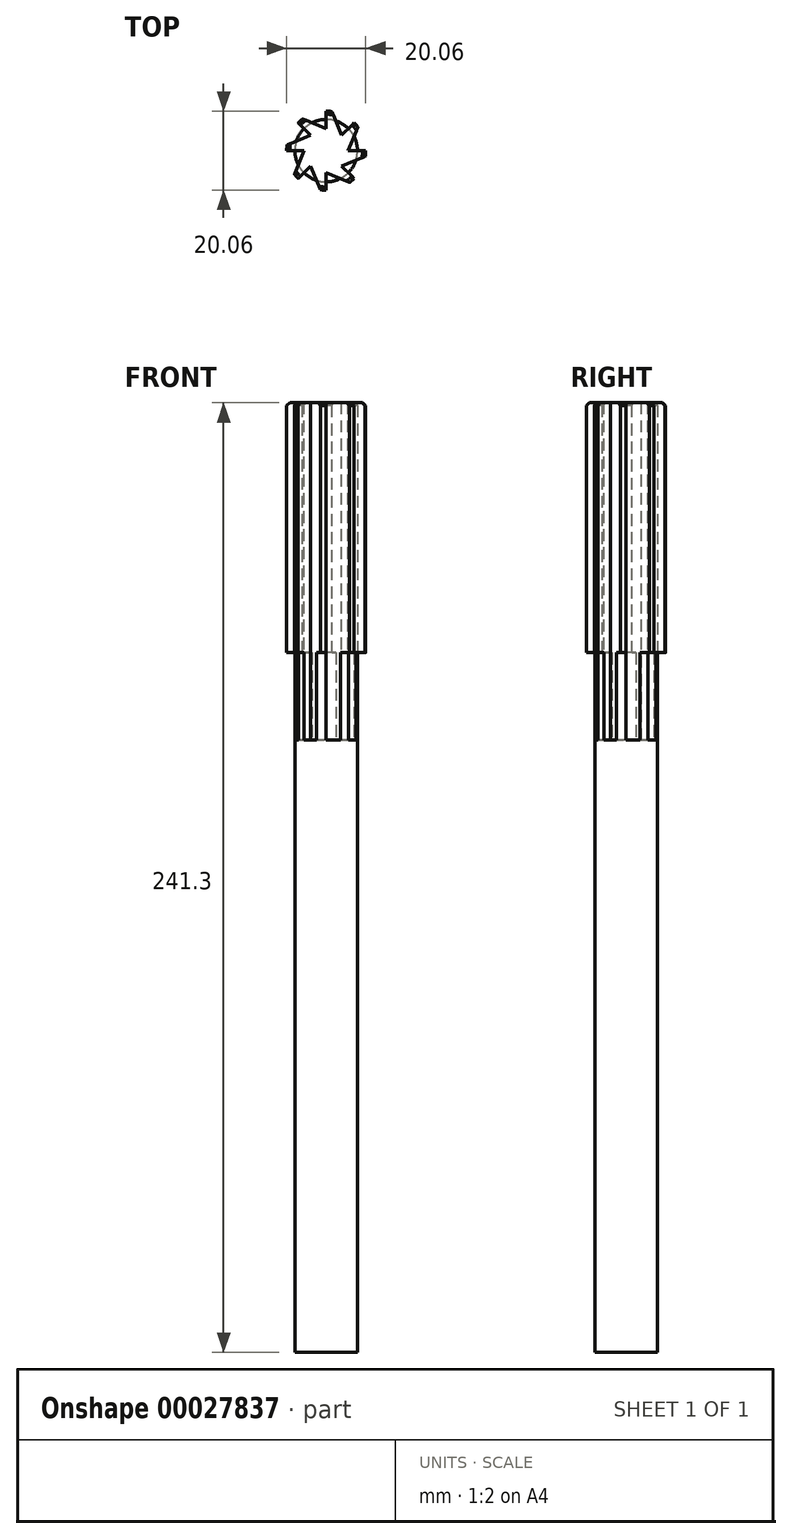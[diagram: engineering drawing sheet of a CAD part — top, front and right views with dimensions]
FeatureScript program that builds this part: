
annotation { "Feature Type Name" : "Feature", "Feature Type Description" : "" }
export const myFeature = defineFeature(function(context is Context, id is Id, definition is map)
    precondition{}
    {
        {
            var Q0;
            Q0=qCreatedBy(makeId("Top.planeOp"),FACE);
            var sketch = newSketch(context, id + "F0", { "sketchPlane" : qUnion([Q0])});
            skCircle(sketch, "E0", {"center": v(0, 0) * mm, "radius": 7.94 * mm});
            skSolve(sketch);
        }
        {
            var Q0;
            Q0 = qSketchRegion(id + "F0", true);
            extrude(context, id + "F1", {"entities" : qUnion([Q0]), "endBound" : BoundingType.SYMMETRIC, "depth" : 241.3 * mm});
        }
        {
            var Q0;
            Q0=makeQuery(id+"F1.opExtrude","CAP_FACE",FACE,{"disambiguationData":[OSD([sQuery(id+"F0.wireOp",EDGE,"E0")])],"isStart":false});
            var sketch = newSketch(context, id + "F2", { "sketchPlane" : qUnion([Q0])});
            skCircle(sketch, "E1", {"center": v(0, 0) * mm, "radius": 10.03 * mm});
            skSolve(sketch);
        }
        {
            var Q0;
            Q0 = qSketchRegion(id + "F2", true);
            extrude(context, id + "F3", {"entities" : qUnion([Q0]), "operationType" : NewBodyOperationType.ADD, "oppositeDirection" : true, "depth" : 63.5 * mm});
        }
        {
            var Q0;
            Q0=makeQuery(id+"F3.boolean.opBoolean","MERGE",FACE,{"derivedFrom":[makeQuery(id+"F1.opExtrude","CAP_FACE",FACE,{"disambiguationData":[OSD([sQuery(id+"F0.wireOp",EDGE,"E0")])],"isStart":false}),makeQuery(id+"F3.opExtrude","CAP_FACE",FACE,{"disambiguationData":[OSD([sQuery(id+"F2.wireOp",EDGE,"E1")])],"isStart":true})]});
            var sketch = newSketch(context, id + "F4", { "sketchPlane" : qUnion([Q0])});
            skLineSegment(sketch, "E2", {"start": v(0, 5.58) * mm, "end": v(0, 12.7) * mm});
            skLineSegment(sketch, "E3", {"start": v(0.33, 12.7) * mm, "end": v(3.95, 3.95) * mm});
            skArc(sketch, "E4", {"start": v(8.98, 8.98) * mm, "mid": v(5.01, 11.67) * mm, "end": v(0.33, 12.7) * mm});
            skLineSegment(sketch, "E5.1.0", {"start": v(-8.75, 9.2) * mm, "end": v(0, 5.58) * mm});
            skLineSegment(sketch, "E5.1.1", {"start": v(-3.95, 3.95) * mm, "end": v(-8.98, 8.98) * mm});
            skLineSegment(sketch, "E5.2.0", {"start": v(-12.7, 0.33) * mm, "end": v(-3.95, 3.95) * mm});
            skLineSegment(sketch, "E5.2.1", {"start": v(-5.58, 0) * mm, "end": v(-12.7, 0) * mm});
            skLineSegment(sketch, "E5.3.0", {"start": v(-9.2, -8.75) * mm, "end": v(-5.58, 0) * mm});
            skLineSegment(sketch, "E5.3.1", {"start": v(-3.95, -3.95) * mm, "end": v(-8.98, -8.98) * mm});
            skLineSegment(sketch, "E5.4.0", {"start": v(-0.33, -12.7) * mm, "end": v(-3.95, -3.95) * mm});
            skLineSegment(sketch, "E5.4.1", {"start": v(0, -5.58) * mm, "end": v(0, -12.7) * mm});
            skLineSegment(sketch, "E5.5.0", {"start": v(8.75, -9.2) * mm, "end": v(0, -5.58) * mm});
            skLineSegment(sketch, "E5.5.1", {"start": v(3.95, -3.95) * mm, "end": v(8.98, -8.98) * mm});
            skLineSegment(sketch, "E5.6.0", {"start": v(12.7, -0.33) * mm, "end": v(3.95, -3.95) * mm});
            skLineSegment(sketch, "E5.6.1", {"start": v(5.58, 0) * mm, "end": v(12.7, 0) * mm});
            skLineSegment(sketch, "E5.7.0", {"start": v(9.2, 8.75) * mm, "end": v(5.58, 0) * mm});
            skLineSegment(sketch, "E5.7.1", {"start": v(3.95, 3.95) * mm, "end": v(8.98, 8.98) * mm});
            skPoint(sketch, "E6.orphan", {"position": v(-5.58, 0) * mm});
            skArc(sketch, "E7.trimOffspring", {"start": v(-12.7, 0) * mm, "mid": v(-11.8, -4.7) * mm, "end": v(-9.2, -8.75) * mm});
            skArc(sketch, "E8.trimOffspring", {"start": v(0, 12.7) * mm, "mid": v(-4.7, 11.8) * mm, "end": v(-8.75, 9.2) * mm});
            skArc(sketch, "E9.trimOffspring", {"start": v(-8.98, 8.98) * mm, "mid": v(-11.67, 5.01) * mm, "end": v(-12.7, 0.33) * mm});
            skArc(sketch, "E10.trimOffspring", {"start": v(12.7, 0) * mm, "mid": v(11.8, 4.7) * mm, "end": v(9.2, 8.75) * mm});
            skArc(sketch, "E11.trimOffspring", {"start": v(8.98, -8.98) * mm, "mid": v(11.67, -5.01) * mm, "end": v(12.7, -0.33) * mm});
            skArc(sketch, "E12.trimOffspring", {"start": v(0, -12.7) * mm, "mid": v(4.7, -11.8) * mm, "end": v(8.75, -9.2) * mm});
            skArc(sketch, "E13.trimOffspring", {"start": v(-8.98, -8.98) * mm, "mid": v(-5.01, -11.67) * mm, "end": v(-0.33, -12.7) * mm});
            skLineSegment(sketch, "E14", {"start": v(3.95, 3.95) * mm, "end": v(5.58, 0) * mm, "construction": true});
            skSolve(sketch);
        }
        {
            var Q0;
            Q0 = qSketchRegion(id + "F4", true);
            extrude(context, id + "F5", {"entities" : qUnion([Q0]), "operationType" : NewBodyOperationType.REMOVE, "oppositeDirection" : true, "depth" : 85.72 * mm});
        }
        {
            var Q0;
            {var subQ0=sQuery(id+"F2.wireOp",EDGE,"E1");Q0=makeQuery(id+"F5.boolean.opBoolean","SPLIT",EDGE,{"disambiguationData":[TD([makeQuery(id+"F5.opExtrude","SWEPT_FACE",FACE,{"disambiguationData":[OSD([sQuery(id+"F4.wireOp",EDGE,"E5.1.0")])]})])],"derivedFrom":makeQuery(id+"F3.opExtrude","CAP_EDGE",EDGE,{"disambiguationData":[OSD([subQ0])],"isStart":true})});}
            var Q1;
            {var subQ0=sQuery(id+"F2.wireOp",EDGE,"E1");Q1=makeQuery(id+"F5.boolean.opBoolean","SPLIT",EDGE,{"disambiguationData":[TD([makeQuery(id+"F5.opExtrude","SWEPT_FACE",FACE,{"disambiguationData":[OSD([sQuery(id+"F4.wireOp",EDGE,"E5.2.0")])]})])],"derivedFrom":makeQuery(id+"F3.opExtrude","CAP_EDGE",EDGE,{"disambiguationData":[OSD([subQ0])],"isStart":true})});}
            var Q2;
            {var subQ0=sQuery(id+"F2.wireOp",EDGE,"E1");Q2=makeQuery(id+"F5.boolean.opBoolean","SPLIT",EDGE,{"disambiguationData":[TD([makeQuery(id+"F5.opExtrude","SWEPT_FACE",FACE,{"disambiguationData":[OSD([sQuery(id+"F4.wireOp",EDGE,"E2")])]})])],"derivedFrom":makeQuery(id+"F3.opExtrude","CAP_EDGE",EDGE,{"disambiguationData":[OSD([subQ0])],"isStart":true})});}
            var Q3;
            {var subQ0=sQuery(id+"F2.wireOp",EDGE,"E1");Q3=makeQuery(id+"F5.boolean.opBoolean","SPLIT",EDGE,{"disambiguationData":[TD([makeQuery(id+"F5.opExtrude","SWEPT_FACE",FACE,{"disambiguationData":[OSD([sQuery(id+"F4.wireOp",EDGE,"E5.7.0")])]})])],"derivedFrom":makeQuery(id+"F3.opExtrude","CAP_EDGE",EDGE,{"disambiguationData":[OSD([subQ0])],"isStart":true})});}
            var Q4;
            {var subQ0=sQuery(id+"F2.wireOp",EDGE,"E1");Q4=makeQuery(id+"F5.boolean.opBoolean","SPLIT",EDGE,{"disambiguationData":[TD([makeQuery(id+"F5.opExtrude","SWEPT_FACE",FACE,{"disambiguationData":[OSD([sQuery(id+"F4.wireOp",EDGE,"E5.6.0")])]})])],"derivedFrom":makeQuery(id+"F3.opExtrude","CAP_EDGE",EDGE,{"disambiguationData":[OSD([subQ0])],"isStart":true})});}
            var Q5;
            {var subQ0=sQuery(id+"F2.wireOp",EDGE,"E1");Q5=makeQuery(id+"F5.boolean.opBoolean","SPLIT",EDGE,{"disambiguationData":[TD([makeQuery(id+"F5.opExtrude","SWEPT_FACE",FACE,{"disambiguationData":[OSD([sQuery(id+"F4.wireOp",EDGE,"E5.5.0")])]})])],"derivedFrom":makeQuery(id+"F3.opExtrude","CAP_EDGE",EDGE,{"disambiguationData":[OSD([subQ0])],"isStart":true})});}
            var Q6;
            {var subQ0=sQuery(id+"F2.wireOp",EDGE,"E1");Q6=makeQuery(id+"F5.boolean.opBoolean","SPLIT",EDGE,{"disambiguationData":[TD([makeQuery(id+"F5.opExtrude","SWEPT_FACE",FACE,{"disambiguationData":[OSD([sQuery(id+"F4.wireOp",EDGE,"E5.4.0")])]})])],"derivedFrom":makeQuery(id+"F3.opExtrude","CAP_EDGE",EDGE,{"disambiguationData":[OSD([subQ0])],"isStart":true})});}
            var Q7;
            {var subQ0=sQuery(id+"F2.wireOp",EDGE,"E1");Q7=makeQuery(id+"F5.boolean.opBoolean","SPLIT",EDGE,{"disambiguationData":[TD([makeQuery(id+"F5.opExtrude","SWEPT_FACE",FACE,{"disambiguationData":[OSD([sQuery(id+"F4.wireOp",EDGE,"E5.3.0")])]})])],"derivedFrom":makeQuery(id+"F3.opExtrude","CAP_EDGE",EDGE,{"disambiguationData":[OSD([subQ0])],"isStart":true})});}
            chamfer(context, id + "F6", {"entities" : qUnion([Q0, Q1, Q2, Q3, Q4, Q5, Q6, Q7]), "width" : 0.8 * mm, "tangentPropagation" : true});
        }
    });
